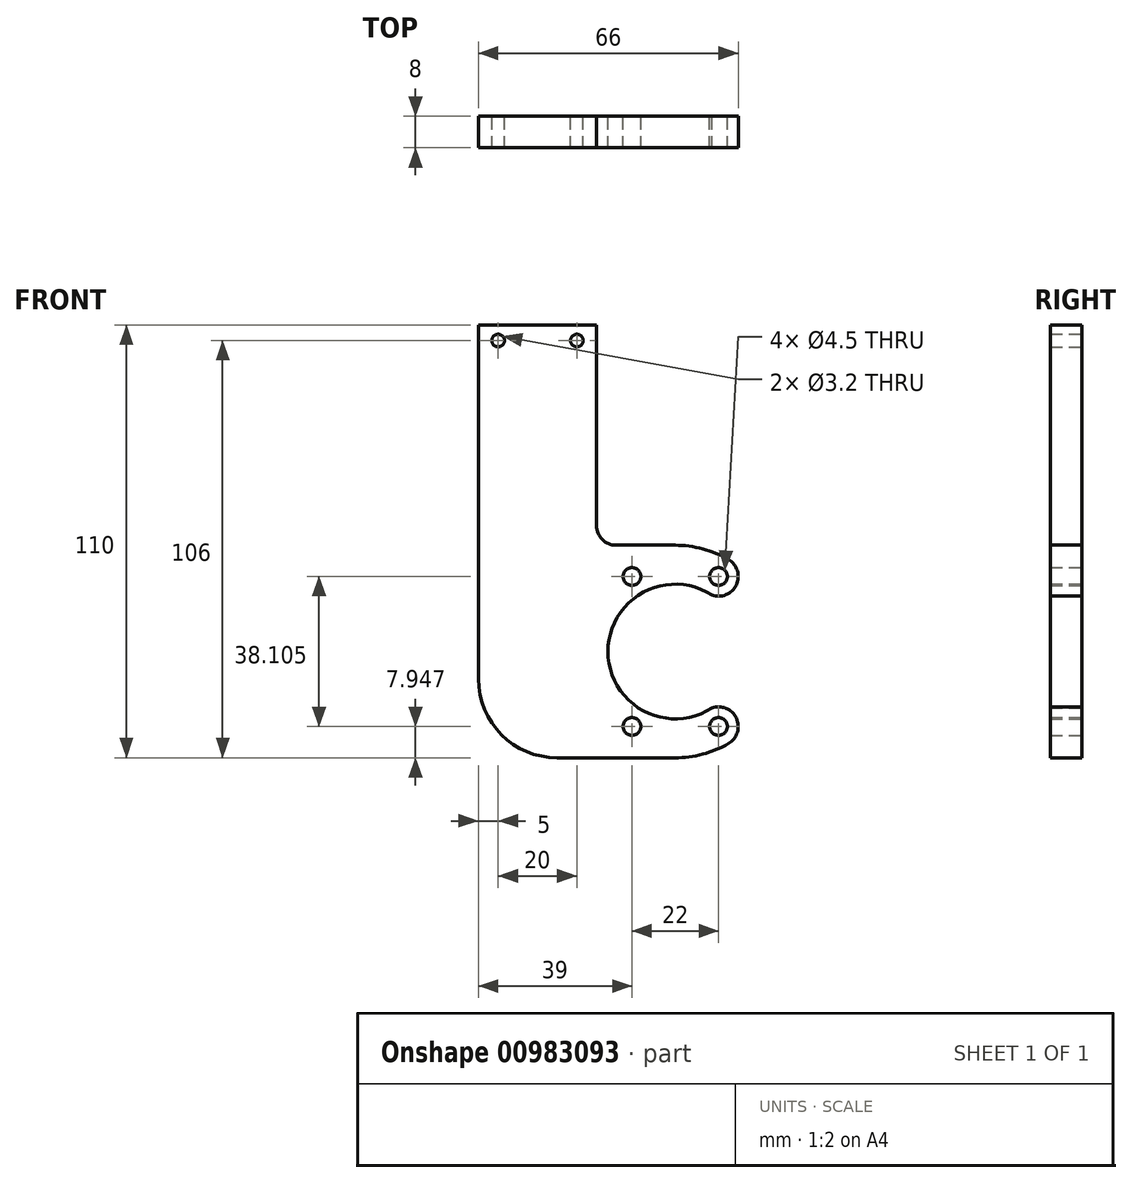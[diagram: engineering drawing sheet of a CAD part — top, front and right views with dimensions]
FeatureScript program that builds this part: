
annotation { "Feature Type Name" : "Feature", "Feature Type Description" : "" }
export const myFeature = defineFeature(function(context is Context, id is Id, definition is map)
    precondition{}
    {
        {
            var Q0;
            Q0=qCreatedBy(makeId("Front.planeOp"),FACE);
            var sketch = newSketch(context, id + "F0", { "sketchPlane" : qUnion([Q0])});
            skArc(sketch, "E0", {"start": v(9.3, 14.35) * mm, "mid": v(-17.1, 0) * mm, "end": v(9.3, -14.35) * mm});
            skArc(sketch, "E1", {"start": v(-12.89, -17.83) * mm, "mid": v(0, -22) * mm, "end": v(12.89, -17.83) * mm, "construction": true});
            skLineSegment(sketch, "E2", {"start": v(0, 0) * mm, "end": v(-13.5, 23.38) * mm, "construction": true});
            skLineSegment(sketch, "E3", {"start": v(0, 0) * mm, "end": v(-13.5, -23.38) * mm, "construction": true});
            skLineSegment(sketch, "E4", {"start": v(0, 0) * mm, "end": v(13.5, -23.38) * mm, "construction": true});
            skLineSegment(sketch, "E5", {"start": v(0, 0) * mm, "end": v(13.5, 23.38) * mm, "construction": true});
            skCircle(sketch, "E6", {"center": v(-11, 19.05) * mm, "radius": 2.25 * mm});
            skCircle(sketch, "E7", {"center": v(11, 19.05) * mm, "radius": 2.25 * mm});
            skCircle(sketch, "E8", {"center": v(-11, -19.05) * mm, "radius": 2.25 * mm});
            skCircle(sketch, "E9", {"center": v(11, -19.05) * mm, "radius": 2.25 * mm});
            skArc(sketch, "E10", {"start": v(0, -27) * mm, "mid": v(6.99, -26.08) * mm, "end": v(13.5, -23.38) * mm});
            skArc(sketch, "E11.trimOffspring", {"start": v(13.5, 23.38) * mm, "mid": v(6.99, 26.08) * mm, "end": v(0, 27) * mm});
            skLineSegment(sketch, "E12.bottom", {"start": v(-15, 32) * mm, "end": v(65, 32) * mm, "construction": true});
            skLineSegment(sketch, "E12.top", {"start": v(-15, 72) * mm, "end": v(65, 72) * mm, "construction": true});
            skLineSegment(sketch, "E12.left", {"start": v(-15, 32) * mm, "end": v(-15, 72) * mm, "construction": true});
            skLineSegment(sketch, "E12.right", {"start": v(65, 32) * mm, "end": v(65, 72) * mm, "construction": true});
            skPoint(sketch, "E12.middle", {"position": v(25, 52) * mm});
            skArc(sketch, "E13.trimOffspring", {"start": v(12.89, 17.83) * mm, "mid": v(0, 22) * mm, "end": v(-12.89, 17.83) * mm, "construction": true});
            skLineSegment(sketch, "E14.bottom", {"start": v(-50, 83) * mm, "end": v(-20, 83) * mm});
            skLineSegment(sketch, "E14.left", {"start": v(-50, 83) * mm, "end": v(-50, -7) * mm});
            skLineSegment(sketch, "E14.right", {"start": v(-20, 83) * mm, "end": v(-20, 32) * mm});
            skLineSegment(sketch, "E15", {"start": v(0, 27) * mm, "end": v(-15, 27) * mm});
            skPoint(sketch, "E16.visualSharp", {"position": v(-20, 27) * mm});
            skArc(sketch, "E16.filletArc", {"start": v(-20, 32) * mm, "mid": v(-18.54, 28.46) * mm, "end": v(-15, 27) * mm});
            skLineSegment(sketch, "E17", {"start": v(0, -27) * mm, "end": v(-30, -27) * mm});
            skArc(sketch, "E18", {"start": v(9.3, 14.35) * mm, "mid": v(15.53, 16.94) * mm, "end": v(13.5, 23.38) * mm});
            skArc(sketch, "E19", {"start": v(13.5, -23.38) * mm, "mid": v(15.53, -16.94) * mm, "end": v(9.3, -14.35) * mm});
            skPoint(sketch, "E20.visualSharp", {"position": v(-50, -27) * mm});
            skArc(sketch, "E20.filletArc", {"start": v(-50, -7) * mm, "mid": v(-44.14, -21.14) * mm, "end": v(-30, -27) * mm});
            skCircle(sketch, "E21", {"center": v(-45, 79) * mm, "radius": 1.6 * mm});
            skCircle(sketch, "E22", {"center": v(-25, 79) * mm, "radius": 1.6 * mm});
            skSolve(sketch);
        }
        {
            var Q0;
            Q0 = qSketchRegion(id + "F0", true);
            extrude(context, id + "F1", {"entities" : qUnion([Q0]), "depth" : 8 * mm, "offsetDistance" : 25 * mm});
        }
    });
